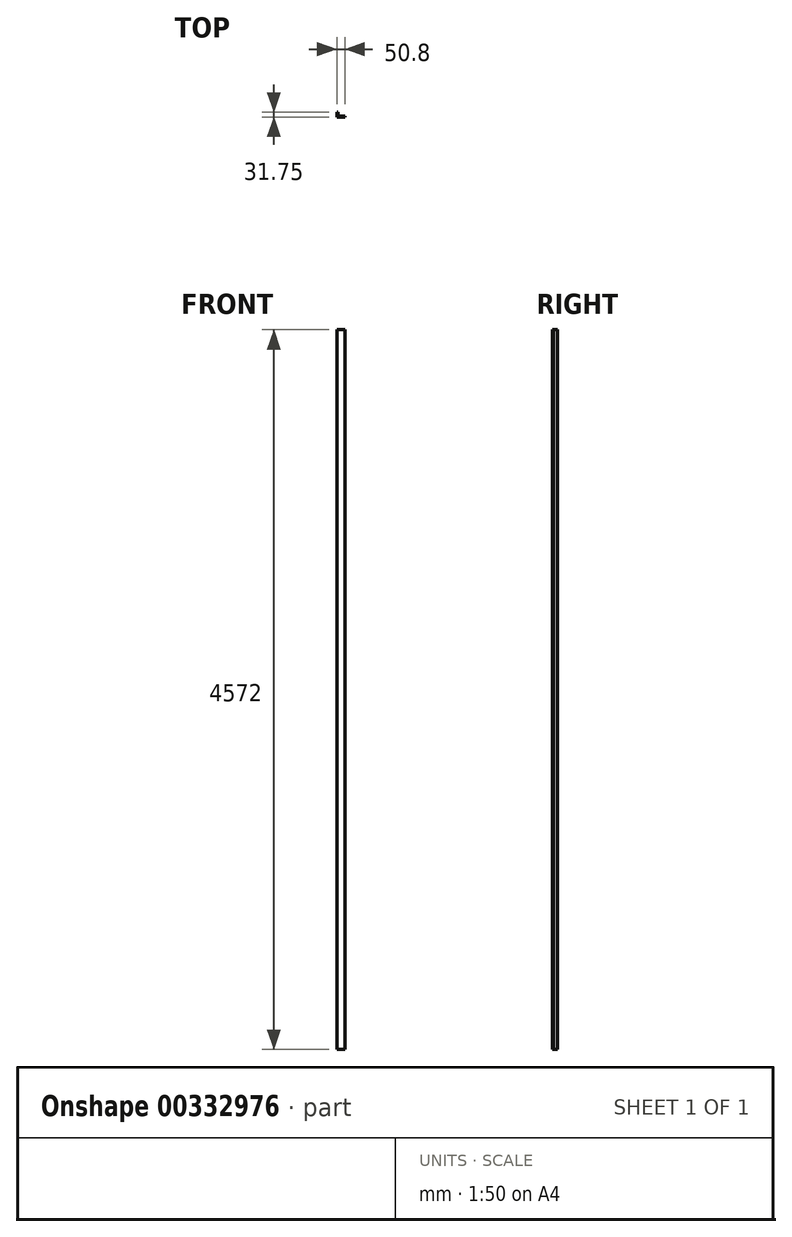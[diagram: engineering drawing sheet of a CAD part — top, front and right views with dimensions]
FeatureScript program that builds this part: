
annotation { "Feature Type Name" : "Feature", "Feature Type Description" : "" }
export const myFeature = defineFeature(function(context is Context, id is Id, definition is map)
    precondition{}
    {
        {
            var Q0;
            Q0=qCreatedBy(makeId("Top.planeOp"),FACE);
            var sketch = newSketch(context, id + "F0", { "sketchPlane" : qUnion([Q0])});
            skLineSegment(sketch, "E0", {"start": v(0, 0) * mm, "end": v(0, 31.75) * mm});
            skLineSegment(sketch, "E1", {"start": v(0, 31.75) * mm, "end": v(6.35, 31.75) * mm});
            skLineSegment(sketch, "E2", {"start": v(6.35, 31.75) * mm, "end": v(6.35, 6.35) * mm});
            skLineSegment(sketch, "E3", {"start": v(6.35, 6.35) * mm, "end": v(50.8, 6.35) * mm});
            skLineSegment(sketch, "E4", {"start": v(50.8, 6.35) * mm, "end": v(50.8, 0) * mm});
            skLineSegment(sketch, "E5", {"start": v(50.8, 0) * mm, "end": v(0, 0) * mm});
            skSolve(sketch);
        }
        {
            var Q0;
            Q0=makeQuery(id+"F0.imprint","IMPRINT",FACE,{"disambiguationData":[TD([[makeQuery(id+"F0.imprint","IMPRINT",EDGE,{"derivedFrom":sQuery(id+"F0.wireOp",EDGE,"E0")}),-1.0]])]});
            extrude(context, id + "F1", {"entities" : qUnion([Q0]), "oppositeDirection" : true, "depth" : 4572 * mm});
        }
    });
